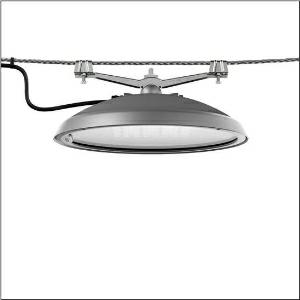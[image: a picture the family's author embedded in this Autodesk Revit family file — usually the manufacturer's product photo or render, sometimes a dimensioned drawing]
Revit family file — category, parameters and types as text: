
# Revit family: dl_r__50_iq_mini___st0_8s_5xa248v41f08fe_e25f
name_source: partatom
category: Lighting Fixtures
units: mm (PartAtom-declared; Revit-internal decimal feet)

## family parameters
Cut with Voids When Loaded = No
Host = Face
Light Source = No
Part Type = Normal
Room Calculation Point = No
Round Connector Dimension = Use Diameter
Shared = No

## types (1)
- --- (1 x LED, 2690 lm, 15.7 W, 4000K)
    Apparent Load = 16 VA
    CIE Flux Codes = 38 75 97 100 100
    Color Rendering = 70
    Color Temperature = 4000K
    Default Elevation = 1800 mm
    Description = DL® 50 iQ mini, catenary luminaire, primary light control with lens, of PMMA, primary optical cover: cover, of toughened safety glass, transparent, light distribution: ST0.8s, light emission: direct distribution, primary light characteristic: symmetric, installation type: suspended mounting, LED, High Power LED, rated luminous flux: 2.690lm, luminous efficacy: 171lm/W, light colour: 740, colour temperature: 4000K, control gear: iQ Street-Remote, control: optimised constant luminous flux control (CLO 2.0), Desk-Remote (wireless, voltage-free reading and setting of iQ features in the workshop via application-optimized NFC function/RFID function), Light-Fading, Smart-Wire, Night-Set, Lumen-Switch, Temp-Guard, Auto-Match, Street-Remote, mains connection: 230..240V, AC, 50/60Hz, start of lifetime: 16W, end of service life: 16W, reduction: 8W, luminaire housing, of diecast aluminium, powder-coated, Siteco® metallic grey (DB 702S), diameter: 500mm, height: 115mm, mounting height: 4..12m, protection rating (complete): IP66, insulation class (complete): insulation class II (safety insulation), certification: CE, ENEC, ENEC+, VDE, impact resistance: IK08, permissible operating ambient temperature for outdoor applications: -25..+40°C, standard-compliant lighting for roads and squares, packaging unit: 1 piece

Light Distribution: ST0.8s
    Height = 124 mm  [stored 0.406824 ft]
    Lamp = 1 x LED
    Lamp Light Flux = 2690 lm
    Lamp Power = 15.7 W
    Lamp count = 1
    Length = 500 mm
    Luminous efficacy = 171 lm/W
    Manufacturer = Siteco
    ModVariant = No
    Model = 5XA248V41F08FE
    Number of Poles = 1
    OnlyDefault = Yes
    Power Factor = 1
    Product Name = DL® 50 iQ mini | ST0.8s
    Product group = catenary luminaire
    ProductGroupID = 6300
    Protection Class = Protection class II
    Protection Degree = IP 66
    RLX_Detail_Level = 1
    RLX_Emergency_Light_Flux = 0 lm
    RLX_Emergency_Type = 0
    RLX_Emergency_Type_DB = No
    RlxData = <blob elided: 123337 chars, md5=09219ba6>
    Socket = socket
    Standby Power = 0 W
    System Light Flux = 2690 lm
    System Power = 16 W
    Type Comments = factory setting: luminous flux: 100 % | dim-lin: 254 | 319 mA
    Type Image = l_1242791.jpg
    URL = http://relux.com
    VarID = @adj_159411
    Voltage = 0 V
    Weight = 0.00 kg
    Width = 0 mm  [stored 0 ft]

note: [stored X ft] marks values corroborated as IEEE doubles in the binary element streams (Revit-internal decimal feet)

## geometry (parser evidence)
native form markers: Blend x4, Sweep x13
no freeform markers — native parametric forms only
